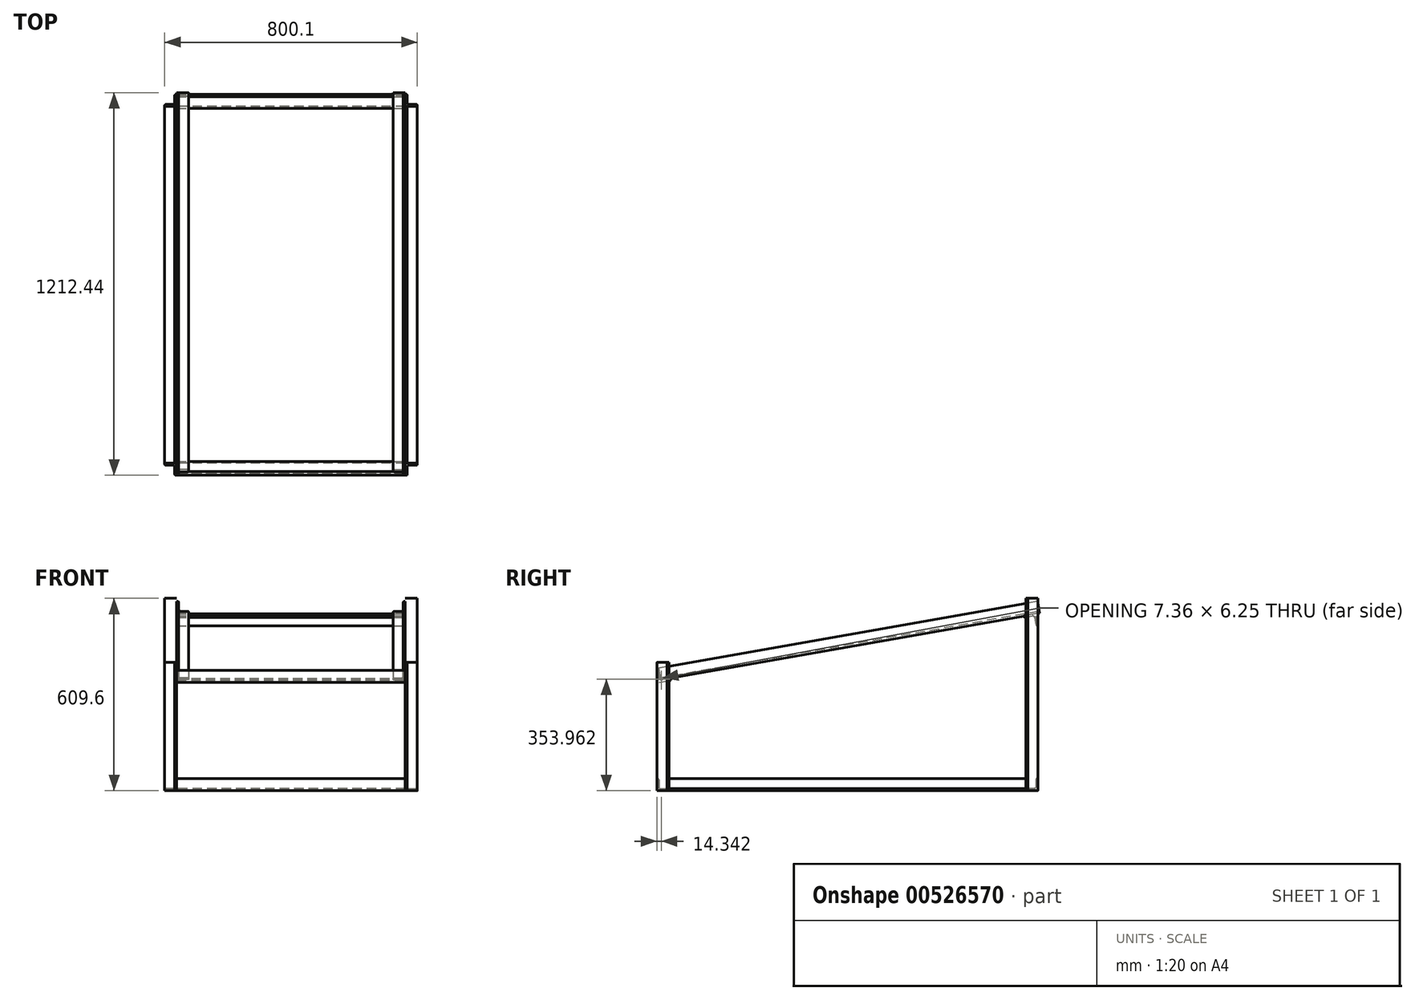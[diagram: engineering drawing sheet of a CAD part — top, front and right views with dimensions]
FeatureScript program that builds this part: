
annotation { "Feature Type Name" : "Feature", "Feature Type Description" : "" }
export const myFeature = defineFeature(function(context is Context, id is Id, definition is map)
    precondition{}
    {
        {
            var Q0;
            Q0=qCreatedBy(makeId("Right.planeOp"),FACE);
            var sketch = newSketch(context, id + "F0", { "sketchPlane" : qUnion([Q0])});
            skLineSegment(sketch, "E0.bottom", {"start": v(0, 0) * mm, "end": v(38.1, 0) * mm});
            skLineSegment(sketch, "E0.top", {"start": v(0, 406.4) * mm, "end": v(38.1, 406.4) * mm});
            skLineSegment(sketch, "E0.left", {"start": v(0, 0) * mm, "end": v(0, 406.4) * mm});
            skLineSegment(sketch, "E0.right", {"start": v(38.1, 0) * mm, "end": v(38.1, 406.4) * mm});
            skLineSegment(sketch, "E1.bottom", {"start": v(1168.4, 0) * mm, "end": v(1206.5, 0) * mm});
            skLineSegment(sketch, "E1.top", {"start": v(1168.4, 609.6) * mm, "end": v(1206.5, 609.6) * mm});
            skLineSegment(sketch, "E1.left", {"start": v(1168.4, 0) * mm, "end": v(1168.4, 609.6) * mm});
            skLineSegment(sketch, "E1.right", {"start": v(1206.5, 0) * mm, "end": v(1206.5, 609.6) * mm});
            skLineSegment(sketch, "E2", {"start": v(62.09, 495.12) * mm, "end": v(1137.7, 684.77) * mm, "construction": true});
            skLineSegment(sketch, "E3", {"start": v(62.09, 495.12) * mm, "end": v(-12.9, 920.36) * mm, "construction": true});
            skLineSegment(sketch, "E4", {"start": v(-12.9, 920.36) * mm, "end": v(1062.72, 1110.01) * mm, "construction": true});
            skLineSegment(sketch, "E5", {"start": v(1062.72, 1110.01) * mm, "end": v(1137.7, 684.77) * mm, "construction": true});
            skLineSegment(sketch, "E6", {"start": v(16.46, 351.66) * mm, "end": v(1229.64, 565.58) * mm});
            skLineSegment(sketch, "E7", {"start": v(1229.64, 565.58) * mm, "end": v(1204.28, 709.41) * mm});
            skLineSegment(sketch, "E8", {"start": v(1204.28, 709.41) * mm, "end": v(-8.9, 495.5) * mm});
            skLineSegment(sketch, "E9", {"start": v(-8.9, 495.5) * mm, "end": v(16.46, 351.66) * mm});
            skLineSegment(sketch, "E10", {"start": v(6.8, 378.98) * mm, "end": v(10.94, 355.53) * mm});
            skLineSegment(sketch, "E11", {"start": v(16.46, 351.66) * mm, "end": v(39.9, 355.8) * mm});
            skLineSegment(sketch, "E12", {"start": v(43.59, 353.22) * mm, "end": v(44.14, 350.1) * mm});
            skLineSegment(sketch, "E13", {"start": v(44.14, 350.1) * mm, "end": v(6.62, 343.48) * mm});
            skLineSegment(sketch, "E14", {"start": v(6.62, 343.48) * mm, "end": v(0, 381) * mm});
            skLineSegment(sketch, "E15", {"start": v(0, 381) * mm, "end": v(3.13, 381.55) * mm});
            skPoint(sketch, "E16.visualSharp", {"position": v(11.77, 350.84) * mm});
            skArc(sketch, "E16.filletArc", {"start": v(10.94, 355.53) * mm, "mid": v(12.9, 352.45) * mm, "end": v(16.46, 351.66) * mm});
            skPoint(sketch, "E17.visualSharp", {"position": v(43.03, 356.35) * mm});
            skArc(sketch, "E17.filletArc", {"start": v(43.59, 353.22) * mm, "mid": v(42.28, 355.27) * mm, "end": v(39.9, 355.8) * mm});
            skPoint(sketch, "E18.visualSharp", {"position": v(6.25, 382.1) * mm});
            skArc(sketch, "E18.filletArc", {"start": v(6.8, 378.98) * mm, "mid": v(5.5, 381.03) * mm, "end": v(3.13, 381.55) * mm});
            skLineSegment(sketch, "E19", {"start": v(1162.36, 553.72) * mm, "end": v(1199.88, 560.33) * mm});
            skLineSegment(sketch, "E20", {"start": v(1199.88, 560.33) * mm, "end": v(1206.5, 522.81) * mm});
            skLineSegment(sketch, "E21", {"start": v(1206.5, 522.81) * mm, "end": v(1204.94, 522.54) * mm});
            skLineSegment(sketch, "E22", {"start": v(1201.26, 525.11) * mm, "end": v(1197.12, 548.56) * mm});
            skLineSegment(sketch, "E23", {"start": v(1189.77, 553.71) * mm, "end": v(1166.32, 549.58) * mm});
            skLineSegment(sketch, "E24", {"start": v(1162.64, 552.15) * mm, "end": v(1162.36, 553.72) * mm});
            skPoint(sketch, "E25.visualSharp", {"position": v(1163.19, 549.03) * mm});
            skArc(sketch, "E25.filletArc", {"start": v(1162.64, 552.15) * mm, "mid": v(1163.94, 550.1) * mm, "end": v(1166.32, 549.58) * mm});
            skPoint(sketch, "E26.visualSharp", {"position": v(1201.8, 521.98) * mm});
            skArc(sketch, "E26.filletArc", {"start": v(1201.26, 525.11) * mm, "mid": v(1202.56, 523.06) * mm, "end": v(1204.94, 522.54) * mm});
            skPoint(sketch, "E27.visualSharp", {"position": v(1196.02, 554.81) * mm});
            skArc(sketch, "E27.filletArc", {"start": v(1197.12, 548.56) * mm, "mid": v(1194.51, 552.66) * mm, "end": v(1189.77, 553.71) * mm});
            skLineSegment(sketch, "E28", {"start": v(-8.9, 495.5) * mm, "end": v(-21.03, 564.28) * mm, "construction": true});
            skLineSegment(sketch, "E29", {"start": v(-21.03, 564.28) * mm, "end": v(47.76, 576.41) * mm, "construction": true});
            skLineSegment(sketch, "E30", {"start": v(1204.28, 709.41) * mm, "end": v(1192.15, 778.2) * mm, "construction": true});
            skLineSegment(sketch, "E31", {"start": v(1192.15, 778.2) * mm, "end": v(1123.36, 766.07) * mm, "construction": true});
            skLineSegment(sketch, "E32", {"start": v(38.1, 0) * mm, "end": v(1168.4, 0) * mm, "construction": true});
            skLineSegment(sketch, "E33", {"start": v(603.25, 0) * mm, "end": v(603.25, 455.13) * mm, "construction": true});
            skSolve(sketch);
        }
        {
            var Q0;
            Q0=qCreatedBy(makeId("Top.planeOp"),FACE);
            var sketch = newSketch(context, id + "F1", { "sketchPlane" : qUnion([Q0])});
            skLineSegment(sketch, "E34", {"start": v(-355.6, 0) * mm, "end": v(355.6, 0) * mm, "construction": true});
            skLineSegment(sketch, "E35", {"start": v(361.95, 0) * mm, "end": v(361.95, 38.1) * mm});
            skLineSegment(sketch, "E36", {"start": v(361.95, 38.1) * mm, "end": v(400.05, 38.1) * mm});
            skLineSegment(sketch, "E37", {"start": v(400.05, 38.1) * mm, "end": v(400.05, 34.93) * mm});
            skLineSegment(sketch, "E38", {"start": v(396.88, 31.75) * mm, "end": v(373.06, 31.75) * mm});
            skLineSegment(sketch, "E39", {"start": v(368.3, 26.99) * mm, "end": v(368.3, 3.18) * mm});
            skLineSegment(sketch, "E40", {"start": v(365.13, 0) * mm, "end": v(361.95, 0) * mm});
            skPoint(sketch, "E41.visualSharp", {"position": v(368.3, 31.75) * mm});
            skArc(sketch, "E41.filletArc", {"start": v(373.06, 31.75) * mm, "mid": v(369.7, 30.36) * mm, "end": v(368.3, 26.99) * mm});
            skPoint(sketch, "E42.visualSharp", {"position": v(400.05, 31.75) * mm});
            skArc(sketch, "E42.filletArc", {"start": v(396.88, 31.75) * mm, "mid": v(399.12, 32.68) * mm, "end": v(400.05, 34.93) * mm});
            skPoint(sketch, "E43.visualSharp", {"position": v(368.3, 0) * mm});
            skArc(sketch, "E43.filletArc", {"start": v(365.13, 0) * mm, "mid": v(367.37, 0.93) * mm, "end": v(368.3, 3.18) * mm});
            skLineSegment(sketch, "E44", {"start": v(0, 603.25) * mm, "end": v(711.2, 603.25) * mm, "construction": true});
            skLineSegment(sketch, "E45.MirrorCS", {"start": v(365.13, 1206.5) * mm, "end": v(361.95, 1206.5) * mm});
            skLineSegment(sketch, "E46.MirrorCS", {"start": v(400.05, 1168.4) * mm, "end": v(400.05, 1171.58) * mm});
            skArc(sketch, "E47.MirrorCS", {"start": v(396.88, 1174.75) * mm, "mid": v(399.12, 1173.82) * mm, "end": v(400.05, 1171.58) * mm});
            skArc(sketch, "E48.MirrorCS", {"start": v(365.13, 1206.5) * mm, "mid": v(367.37, 1205.57) * mm, "end": v(368.3, 1203.33) * mm});
            skArc(sketch, "E49.MirrorCS", {"start": v(373.06, 1174.75) * mm, "mid": v(369.7, 1176.14) * mm, "end": v(368.3, 1179.51) * mm});
            skLineSegment(sketch, "E50.MirrorCS", {"start": v(368.3, 1179.51) * mm, "end": v(368.3, 1203.33) * mm});
            skLineSegment(sketch, "E51.MirrorCS", {"start": v(396.88, 1174.75) * mm, "end": v(373.06, 1174.75) * mm});
            skLineSegment(sketch, "E52.MirrorCS", {"start": v(361.95, 1206.5) * mm, "end": v(361.95, 1168.4) * mm});
            skLineSegment(sketch, "E53.MirrorCS", {"start": v(361.95, 1168.4) * mm, "end": v(400.05, 1168.4) * mm});
            skPoint(sketch, "E54.MirrorP", {"position": v(368.3, 1174.75) * mm});
            skPoint(sketch, "E55.MirrorP", {"position": v(400.05, 1174.75) * mm});
            skPoint(sketch, "E56.MirrorP", {"position": v(368.3, 1206.5) * mm});
            skLineSegment(sketch, "E57.MirrorCS", {"start": v(-365.13, 1206.5) * mm, "end": v(-361.95, 1206.5) * mm});
            skLineSegment(sketch, "E58.MirrorCS", {"start": v(-400.05, 1168.4) * mm, "end": v(-400.05, 1171.58) * mm});
            skArc(sketch, "E59.MirrorCS", {"start": v(-365.13, 1206.5) * mm, "mid": v(-367.37, 1205.57) * mm, "end": v(-368.3, 1203.33) * mm});
            skArc(sketch, "E60.MirrorCS", {"start": v(-396.88, 1174.75) * mm, "mid": v(-399.12, 1173.82) * mm, "end": v(-400.05, 1171.58) * mm});
            skArc(sketch, "E61.MirrorCS", {"start": v(-373.06, 1174.75) * mm, "mid": v(-369.7, 1176.14) * mm, "end": v(-368.3, 1179.51) * mm});
            skPoint(sketch, "E62.MirrorP", {"position": v(-400.05, 1174.75) * mm});
            skLineSegment(sketch, "E63.MirrorCS", {"start": v(-396.88, 1174.75) * mm, "end": v(-373.06, 1174.75) * mm});
            skLineSegment(sketch, "E64.MirrorCS", {"start": v(-361.95, 1168.4) * mm, "end": v(-400.05, 1168.4) * mm});
            skPoint(sketch, "E65.MirrorP", {"position": v(-368.3, 1174.75) * mm});
            skPoint(sketch, "E66.MirrorP", {"position": v(-368.3, 1206.5) * mm});
            skLineSegment(sketch, "E67.MirrorCS", {"start": v(-368.3, 1179.51) * mm, "end": v(-368.3, 1203.33) * mm});
            skLineSegment(sketch, "E68.MirrorCS", {"start": v(-361.95, 1206.5) * mm, "end": v(-361.95, 1168.4) * mm});
            skLineSegment(sketch, "E69.MirrorCS", {"start": v(-365.13, 0) * mm, "end": v(-361.95, 0) * mm});
            skLineSegment(sketch, "E70.MirrorCS", {"start": v(-400.05, 38.1) * mm, "end": v(-400.05, 34.93) * mm});
            skArc(sketch, "E71.MirrorCS", {"start": v(-396.88, 31.75) * mm, "mid": v(-399.12, 32.68) * mm, "end": v(-400.05, 34.93) * mm});
            skArc(sketch, "E72.MirrorCS", {"start": v(-365.13, 0) * mm, "mid": v(-367.37, 0.93) * mm, "end": v(-368.3, 3.18) * mm});
            skArc(sketch, "E73.MirrorCS", {"start": v(-373.06, 31.75) * mm, "mid": v(-369.7, 30.36) * mm, "end": v(-368.3, 26.99) * mm});
            skLineSegment(sketch, "E74.MirrorCS", {"start": v(-368.3, 26.99) * mm, "end": v(-368.3, 3.18) * mm});
            skLineSegment(sketch, "E75.MirrorCS", {"start": v(-396.88, 31.75) * mm, "end": v(-373.06, 31.75) * mm});
            skLineSegment(sketch, "E76.MirrorCS", {"start": v(-361.95, 0) * mm, "end": v(-361.95, 38.1) * mm});
            skLineSegment(sketch, "E77.MirrorCS", {"start": v(-361.95, 38.1) * mm, "end": v(-400.05, 38.1) * mm});
            skPoint(sketch, "E78.MirrorP", {"position": v(-368.3, 31.75) * mm});
            skPoint(sketch, "E79.MirrorP", {"position": v(-400.05, 31.75) * mm});
            skPoint(sketch, "E80.MirrorP", {"position": v(-368.3, 0) * mm});
            skSolve(sketch);
        }
        {
            var Q0;
            Q0=makeQuery(id+"F1.imprint","IMPRINT",FACE,{"disambiguationData":[TD([[makeQuery(id+"F1.imprint","IMPRINT",EDGE,{"derivedFrom":sQuery(id+"F1.wireOp",EDGE,"E69.MirrorCS")}),1.0]])]});
            var Q1;
            Q1=makeQuery(id+"F1.imprint","IMPRINT",FACE,{"disambiguationData":[TD([[makeQuery(id+"F1.imprint","IMPRINT",EDGE,{"derivedFrom":sQuery(id+"F1.wireOp",EDGE,"E35")}),-1.0]])]});
            extrude(context, id + "F2", {"entities" : qUnion([Q0, Q1]), "depth" : 406.4 * mm, "offsetDistance" : 25.4 * mm});
        }
        {
            var Q0;
            Q0=makeQuery(id+"F1.imprint","IMPRINT",FACE,{"disambiguationData":[TD([[makeQuery(id+"F1.imprint","IMPRINT",EDGE,{"derivedFrom":sQuery(id+"F1.wireOp",EDGE,"E57.MirrorCS")}),-1.0]])]});
            var Q1;
            Q1=makeQuery(id+"F1.imprint","IMPRINT",FACE,{"disambiguationData":[TD([[makeQuery(id+"F1.imprint","IMPRINT",EDGE,{"derivedFrom":sQuery(id+"F1.wireOp",EDGE,"E45.MirrorCS")}),1.0]])]});
            extrude(context, id + "F3", {"entities" : qUnion([Q0, Q1]), "depth" : 609.6 * mm, "offsetDistance" : 25.4 * mm});
        }
        {
            var Q0;
            Q0=makeQuery(id+"F0.imprint","IMPRINT",FACE,{"disambiguationData":[TD([[makeQuery(id+"F0.imprint","IMPRINT",EDGE,{"derivedFrom":sQuery(id+"F0.wireOp",EDGE,"E10")}),-1.0]])]});
            var Q1;
            {var subQ0=sQuery(id+"F0.wireOp",EDGE,"E20");Q1=makeQuery(id+"F0.imprint","IMPRINT",FACE,{"disambiguationData":[TD([[makeQuery(id+"F0.imprint","IMPRINT",EDGE,{"derivedFrom":subQ0}),-1.0]])]});}
            var Q2;
            {var subQ1=sQuery(id+"F0.wireOp",EDGE,"E12");Q2=makeQuery(id+"F0.imprint","IMPRINT",FACE,{"disambiguationData":[TD([[makeQuery(id+"F0.imprint","IMPRINT",EDGE,{"derivedFrom":subQ1}),-1.0]])]});}
            var Q3;
            {var subQ4=sQuery(id+"F0.wireOp",EDGE,"E24");Q3=makeQuery(id+"F0.imprint","IMPRINT",FACE,{"disambiguationData":[TD([[makeQuery(id+"F0.imprint","IMPRINT",EDGE,{"derivedFrom":subQ4}),-1.0]])]});}
            var Q4;
            Q4=makeQuery(id+"F3.opExtrude","SWEPT_FACE",FACE,{"disambiguationData":[OSD([sQuery(id+"F1.wireOp",EDGE,"E68.MirrorCS")])]});
            var Q5;
            Q5=makeQuery(id+"F3.opExtrude","SWEPT_FACE",FACE,{"disambiguationData":[OSD([sQuery(id+"F1.wireOp",EDGE,"E52.MirrorCS")])]});
            extrude(context, id + "F4", {"entities" : qUnion([Q0, Q1, Q2, Q3]), "endBound" : BoundingType.UP_TO_SURFACE, "oppositeDirection" : true, "depth" : 25.4 * mm, "endBoundEntityFace" : qUnion([Q4]), "offsetDistance" : 25.4 * mm, "hasSecondDirection" : true, "secondDirectionBound" : SecondDirectionBoundingType.UP_TO_SURFACE, "secondDirectionOppositeDirection" : false, "secondDirectionDepth" : 25.4 * mm, "secondDirectionBoundEntityFace" : qUnion([Q5])});
        }
        {
            var Q0;
            Q0=makeQuery(id+"F4.opExtrude","SWEPT_FACE",FACE,{"disambiguationData":[OSD([sQuery(id+"F0.wireOp",EDGE,"E10")])]});
            var sketch = newSketch(context, id + "F5", { "sketchPlane" : qUnion([Q0])});
            skLineSegment(sketch, "E81", {"start": v(-361.95, 381.56) * mm, "end": v(-361.95, 343.46) * mm});
            skLineSegment(sketch, "E82", {"start": v(-361.95, 343.46) * mm, "end": v(-323.85, 343.46) * mm});
            skLineSegment(sketch, "E83", {"start": v(-323.85, 343.46) * mm, "end": v(-323.85, 346.64) * mm});
            skLineSegment(sketch, "E84", {"start": v(-327.03, 349.81) * mm, "end": v(-350.84, 349.81) * mm});
            skLineSegment(sketch, "E85", {"start": v(-355.6, 354.57) * mm, "end": v(-355.6, 378.39) * mm});
            skLineSegment(sketch, "E86", {"start": v(-358.78, 381.56) * mm, "end": v(-361.95, 381.56) * mm});
            skPoint(sketch, "E87.visualSharp", {"position": v(-355.6, 381.56) * mm});
            skArc(sketch, "E87.filletArc", {"start": v(-355.6, 378.39) * mm, "mid": v(-356.53, 380.63) * mm, "end": v(-358.78, 381.56) * mm});
            skPoint(sketch, "E88.visualSharp", {"position": v(-323.85, 349.81) * mm});
            skArc(sketch, "E88.filletArc", {"start": v(-323.85, 346.64) * mm, "mid": v(-324.78, 348.88) * mm, "end": v(-327.03, 349.81) * mm});
            skPoint(sketch, "E89.visualSharp", {"position": v(-355.6, 349.81) * mm});
            skArc(sketch, "E89.filletArc", {"start": v(-355.6, 354.57) * mm, "mid": v(-354.2, 351.2) * mm, "end": v(-350.84, 349.81) * mm});
            skSolve(sketch);
        }
        {
            var Q0;
            Q0 = qSketchRegion(id + "F5", true);
            extrude(context, id + "F6", {"entities" : qUnion([Q0]), "depth" : 1219.2 * mm, "offsetDistance" : 25.4 * mm});
        }
        {
            var Q0;
            Q0=makeQuery(id+"F6.opExtrude","SWEPT_FACE",FACE,{"disambiguationData":[OSD([sQuery(id+"F5.wireOp",EDGE,"E81")])]});
            var sketch = newSketch(context, id + "F7", { "sketchPlane" : qUnion([Q0])});
            skLineSegment(sketch, "E90", {"start": v(11.77, 350.84) * mm, "end": v(18.02, 351.94) * mm});
            skLineSegment(sketch, "E91", {"start": v(18.02, 351.94) * mm, "end": v(10.66, 357.09) * mm});
            skLineSegment(sketch, "E92", {"start": v(10.66, 357.09) * mm, "end": v(11.77, 350.84) * mm});
            skSolve(sketch);
        }
        {
            var Q0;
            Q0 = qSketchRegion(id + "F7", true);
            extrude(context, id + "F8", {"entities" : qUnion([Q0]), "operationType" : NewBodyOperationType.REMOVE, "endBound" : BoundingType.THROUGH_ALL, "oppositeDirection" : true, "depth" : 25.4 * mm, "offsetDistance" : 25.4 * mm});
        }
        {
            var Q0;
            Q0=makeQuery(id+"F6.opExtrude","SWEPT_BODY",BODY,{"disambiguationData":[OSD([sQuery(id+"F5.wireOp",EDGE,"E81"),sQuery(id+"F5.wireOp",EDGE,"E82"),sQuery(id+"F5.wireOp",EDGE,"E83"),sQuery(id+"F5.wireOp",EDGE,"E84"),sQuery(id+"F5.wireOp",EDGE,"E85"),sQuery(id+"F5.wireOp",EDGE,"E86"),sQuery(id+"F5.wireOp",EDGE,"E87.filletArc"),sQuery(id+"F5.wireOp",EDGE,"E88.filletArc"),sQuery(id+"F5.wireOp",EDGE,"E89.filletArc")])]});
            var Q1;
            Q1=qCreatedBy(makeId("Right.planeOp"),FACE);
            mirror(context, id + "F9", {"entities" : qUnion([Q0]), "mirrorPlane" : qUnion([Q1])});
        }
        {
            var Q0;
            Q0=qCreatedBy(makeId("Right.planeOp"),FACE);
            var sketch = newSketch(context, id + "F10", { "sketchPlane" : qUnion([Q0])});
            skLineSegment(sketch, "E93", {"start": v(0, 38.1) * mm, "end": v(0, 0) * mm});
            skLineSegment(sketch, "E94", {"start": v(0, 0) * mm, "end": v(38.1, 0) * mm});
            skLineSegment(sketch, "E95", {"start": v(38.1, 0) * mm, "end": v(38.1, 3.18) * mm});
            skLineSegment(sketch, "E96", {"start": v(34.92, 6.35) * mm, "end": v(11.11, 6.35) * mm});
            skLineSegment(sketch, "E97", {"start": v(6.35, 11.11) * mm, "end": v(6.35, 34.92) * mm});
            skLineSegment(sketch, "E98", {"start": v(3.18, 38.1) * mm, "end": v(0, 38.1) * mm});
            skPoint(sketch, "E99.visualSharp", {"position": v(6.35, 38.1) * mm});
            skArc(sketch, "E99.filletArc", {"start": v(6.35, 34.92) * mm, "mid": v(5.42, 37.17) * mm, "end": v(3.18, 38.1) * mm});
            skPoint(sketch, "E100.visualSharp", {"position": v(38.1, 6.35) * mm});
            skArc(sketch, "E100.filletArc", {"start": v(38.1, 3.18) * mm, "mid": v(37.17, 5.42) * mm, "end": v(34.92, 6.35) * mm});
            skPoint(sketch, "E101.visualSharp", {"position": v(6.35, 6.35) * mm});
            skArc(sketch, "E101.filletArc", {"start": v(6.35, 11.11) * mm, "mid": v(7.74, 7.74) * mm, "end": v(11.11, 6.35) * mm});
            skLineSegment(sketch, "E102.MirrorCS", {"start": v(1168.4, 0) * mm, "end": v(1168.4, 3.18) * mm});
            skArc(sketch, "E103.MirrorCS", {"start": v(1168.4, 3.18) * mm, "mid": v(1169.33, 5.42) * mm, "end": v(1171.58, 6.35) * mm});
            skLineSegment(sketch, "E104.MirrorCS", {"start": v(1203.33, 38.1) * mm, "end": v(1206.5, 38.1) * mm});
            skArc(sketch, "E105.MirrorCS", {"start": v(1200.15, 34.92) * mm, "mid": v(1201.08, 37.17) * mm, "end": v(1203.33, 38.1) * mm});
            skArc(sketch, "E106.MirrorCS", {"start": v(1200.15, 11.11) * mm, "mid": v(1198.76, 7.74) * mm, "end": v(1195.39, 6.35) * mm});
            skLineSegment(sketch, "E107.MirrorCS", {"start": v(1206.5, 38.1) * mm, "end": v(1206.5, 0) * mm});
            skLineSegment(sketch, "E108.MirrorCS", {"start": v(1206.5, 0) * mm, "end": v(1168.4, 0) * mm});
            skLineSegment(sketch, "E109.MirrorCS", {"start": v(1200.15, 11.11) * mm, "end": v(1200.15, 34.92) * mm});
            skLineSegment(sketch, "E110.MirrorCS", {"start": v(1171.58, 6.35) * mm, "end": v(1195.39, 6.35) * mm});
            skPoint(sketch, "E111.MirrorP", {"position": v(1168.4, 6.35) * mm});
            skPoint(sketch, "E112.MirrorP", {"position": v(1200.15, 6.35) * mm});
            skPoint(sketch, "E113.MirrorP", {"position": v(1200.15, 38.1) * mm});
            skSolve(sketch);
        }
        {
            var Q0;
            Q0 = qSketchRegion(id + "F10", true);
            var Q1;
            Q1=makeQuery(id+"F2.opExtrude","SWEPT_FACE",FACE,{"disambiguationData":[OSD([sQuery(id+"F1.wireOp",EDGE,"E35")])]});
            var Q2;
            Q2=makeQuery(id+"F2.opExtrude","SWEPT_FACE",FACE,{"disambiguationData":[OSD([sQuery(id+"F1.wireOp",EDGE,"E76.MirrorCS")])]});
            extrude(context, id + "F11", {"entities" : qUnion([Q0]), "endBound" : BoundingType.UP_TO_SURFACE, "depth" : 25.4 * mm, "endBoundEntityFace" : qUnion([Q1]), "offsetDistance" : 25.4 * mm, "hasSecondDirection" : true, "secondDirectionBound" : SecondDirectionBoundingType.UP_TO_SURFACE, "secondDirectionOppositeDirection" : true, "secondDirectionDepth" : 25.4 * mm, "secondDirectionBoundEntityFace" : qUnion([Q2])});
        }
        {
            var Q0;
            Q0=makeQuery(id+"F3.opExtrude","SWEPT_FACE",FACE,{"disambiguationData":[OSD([sQuery(id+"F1.wireOp",EDGE,"E53.MirrorCS")])]});
            var sketch = newSketch(context, id + "F12", { "sketchPlane" : qUnion([Q0])});
            skLineSegment(sketch, "E114", {"start": v(361.95, 38.1) * mm, "end": v(361.95, 0) * mm});
            skLineSegment(sketch, "E115", {"start": v(361.95, 0) * mm, "end": v(400.05, 0) * mm});
            skLineSegment(sketch, "E116", {"start": v(400.05, 0) * mm, "end": v(400.05, 3.17) * mm});
            skLineSegment(sketch, "E117", {"start": v(396.87, 6.35) * mm, "end": v(373.06, 6.35) * mm});
            skLineSegment(sketch, "E118", {"start": v(368.3, 11.11) * mm, "end": v(368.3, 34.93) * mm});
            skLineSegment(sketch, "E119", {"start": v(365.12, 38.1) * mm, "end": v(361.95, 38.1) * mm});
            skPoint(sketch, "E120.visualSharp", {"position": v(368.3, 38.1) * mm});
            skArc(sketch, "E120.filletArc", {"start": v(368.3, 34.93) * mm, "mid": v(367.37, 37.17) * mm, "end": v(365.12, 38.1) * mm});
            skPoint(sketch, "E121.visualSharp", {"position": v(400.05, 6.35) * mm});
            skArc(sketch, "E121.filletArc", {"start": v(400.05, 3.17) * mm, "mid": v(399.12, 5.42) * mm, "end": v(396.87, 6.35) * mm});
            skPoint(sketch, "E122.visualSharp", {"position": v(368.3, 6.35) * mm});
            skArc(sketch, "E122.filletArc", {"start": v(368.3, 11.11) * mm, "mid": v(369.7, 7.74) * mm, "end": v(373.06, 6.35) * mm});
            skLineSegment(sketch, "E123.MirrorCS", {"start": v(-400.05, 0) * mm, "end": v(-400.05, 3.17) * mm});
            skLineSegment(sketch, "E124.MirrorCS", {"start": v(-365.12, 38.1) * mm, "end": v(-361.95, 38.1) * mm});
            skArc(sketch, "E125.MirrorCS", {"start": v(-368.3, 34.93) * mm, "mid": v(-367.37, 37.17) * mm, "end": v(-365.12, 38.1) * mm});
            skArc(sketch, "E126.MirrorCS", {"start": v(-400.05, 3.17) * mm, "mid": v(-399.12, 5.42) * mm, "end": v(-396.87, 6.35) * mm});
            skArc(sketch, "E127.MirrorCS", {"start": v(-368.3, 11.11) * mm, "mid": v(-369.7, 7.74) * mm, "end": v(-373.06, 6.35) * mm});
            skLineSegment(sketch, "E128.MirrorCS", {"start": v(-368.3, 11.11) * mm, "end": v(-368.3, 34.93) * mm});
            skLineSegment(sketch, "E129.MirrorCS", {"start": v(-396.87, 6.35) * mm, "end": v(-373.06, 6.35) * mm});
            skLineSegment(sketch, "E130.MirrorCS", {"start": v(-361.95, 38.1) * mm, "end": v(-361.95, 0) * mm});
            skLineSegment(sketch, "E131.MirrorCS", {"start": v(-361.95, 0) * mm, "end": v(-400.05, 0) * mm});
            skPoint(sketch, "E132.MirrorP", {"position": v(-368.3, 6.35) * mm});
            skPoint(sketch, "E133.MirrorP", {"position": v(-368.3, 38.1) * mm});
            skPoint(sketch, "E134.MirrorP", {"position": v(-400.05, 6.35) * mm});
            skSolve(sketch);
        }
        {
            var Q0;
            Q0 = qSketchRegion(id + "F12", true);
            var Q1;
            Q1=makeQuery(id+"F2.opExtrude","SWEPT_FACE",FACE,{"disambiguationData":[OSD([sQuery(id+"F1.wireOp",EDGE,"E36")])]});
            extrude(context, id + "F13", {"entities" : qUnion([Q0]), "endBound" : BoundingType.UP_TO_SURFACE, "depth" : 25.4 * mm, "endBoundEntityFace" : qUnion([Q1]), "offsetDistance" : 25.4 * mm});
        }
        {
            var Q0;
            Q0=makeQuery(id+"F4.opExtrude","SWEPT_FACE",FACE,{"disambiguationData":[OSD([sQuery(id+"F0.wireOp",EDGE,"E10")])]});
            var sketch = newSketch(context, id + "F14", { "sketchPlane" : qUnion([Q0])});
            skLineSegment(sketch, "E135", {"start": v(-361.95, 348.22) * mm, "end": v(-298.45, 348.22) * mm});
            skLineSegment(sketch, "E136", {"start": v(-361.95, 348.22) * mm, "end": v(-361.95, 284.72) * mm});
            skLineSegment(sketch, "E137", {"start": v(-298.45, 343.46) * mm, "end": v(-298.45, 348.22) * mm});
            skLineSegment(sketch, "E138", {"start": v(-361.95, 284.72) * mm, "end": v(-357.19, 284.72) * mm});
            skLineSegment(sketch, "E139", {"start": v(-357.19, 284.72) * mm, "end": v(-357.19, 343.46) * mm});
            skLineSegment(sketch, "E140", {"start": v(-357.19, 343.46) * mm, "end": v(-298.45, 343.46) * mm});
            skSolve(sketch);
        }
        {
            var Q0;
            Q0=makeQuery(id+"F4.opExtrude","SWEPT_FACE",FACE,{"disambiguationData":[OSD([sQuery(id+"F0.wireOp",EDGE,"E11")])]});
            var sketch = newSketch(context, id + "F15", { "sketchPlane" : qUnion([Q0])});
            skLineSegment(sketch, "E141.bottom", {"start": v(355.6, 104.26) * mm, "end": v(361.95, 104.26) * mm});
            skLineSegment(sketch, "E141.top", {"start": v(355.6, 77.27) * mm, "end": v(361.95, 77.27) * mm});
            skLineSegment(sketch, "E141.left", {"start": v(355.6, 104.26) * mm, "end": v(355.6, 77.27) * mm});
            skLineSegment(sketch, "E141.right", {"start": v(361.95, 104.26) * mm, "end": v(361.95, 77.27) * mm});
            skLineSegment(sketch, "E142.bottom", {"start": v(361.95, 1267.84) * mm, "end": v(355.6, 1267.84) * mm});
            skLineSegment(sketch, "E142.top", {"start": v(361.95, 1240.86) * mm, "end": v(355.6, 1240.86) * mm});
            skLineSegment(sketch, "E142.left", {"start": v(361.95, 1267.84) * mm, "end": v(361.95, 1240.86) * mm});
            skLineSegment(sketch, "E142.right", {"start": v(355.6, 1267.84) * mm, "end": v(355.6, 1240.86) * mm});
            skSolve(sketch);
        }
    });
